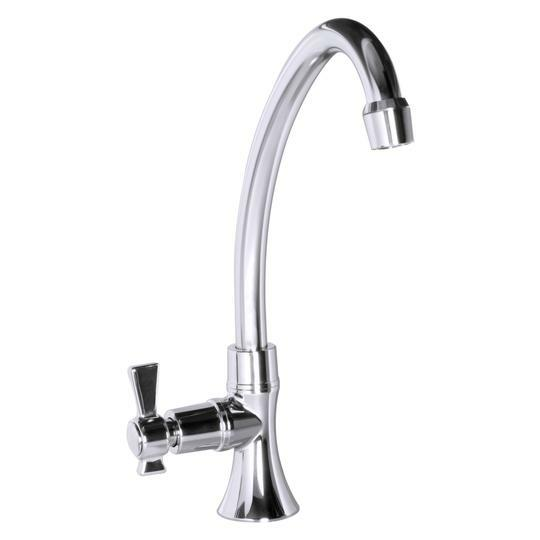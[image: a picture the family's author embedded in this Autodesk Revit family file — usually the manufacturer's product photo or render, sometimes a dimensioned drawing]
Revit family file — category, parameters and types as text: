
# Revit family: 01-1750-11 LLAVE MOVIL MESA LAVAPLATOS CISNE HELIX PALA
name_source: partatom
category: Plumbing Fixtures
revit_build: Autodesk Revit 2018 (Build: 20170223_1515(x64)
units: mm (PartAtom-declared; Revit-internal decimal feet)

## family parameters
Cut with Voids When Loaded = No
Host = Face
OmniClass Number = 23.31.11.00
Part Type = Normal
Room Calculation Point = No
Round Connector Dimension = Use Diameter
Shared = No

## types (1)
- 01-1750-11
    Alto Aireador = 240 mm  [stored 0.787402 ft]
    Alto brazo = 306 mm
    Ancho a manija = 67.12 mm
    Ancho brazo = 160 mm  [stored 0.524934 ft]
    Base = 50 mm
    CW Connection = Yes
    Default Elevation = 0 mm  [stored 0 ft]
    Description = Monomando
    HW Connection = Yes
    Link Ficha Tecnica = No existe
    Manufacturer = Gricol
    Model = 01-1750-11
    Plástico - ABS Cromado = Plastico ABS Cromado
    Product Name = LLAVE MOVIL MESA LAVAPLATOS CISNE HELIX PALA
    Type Image = LLAVE MOVIL MESA LAVAPLATOS CISNE HELIX PALA.jpg
    URL = https://www.gricol.com
    Vent Connection = No
    Waste Connection = No

note: [stored X ft] marks values corroborated as IEEE doubles in the binary element streams (Revit-internal decimal feet)

## geometry (parser evidence)
native form markers: Blend x2, Sweep x6
no freeform markers — native parametric forms only
